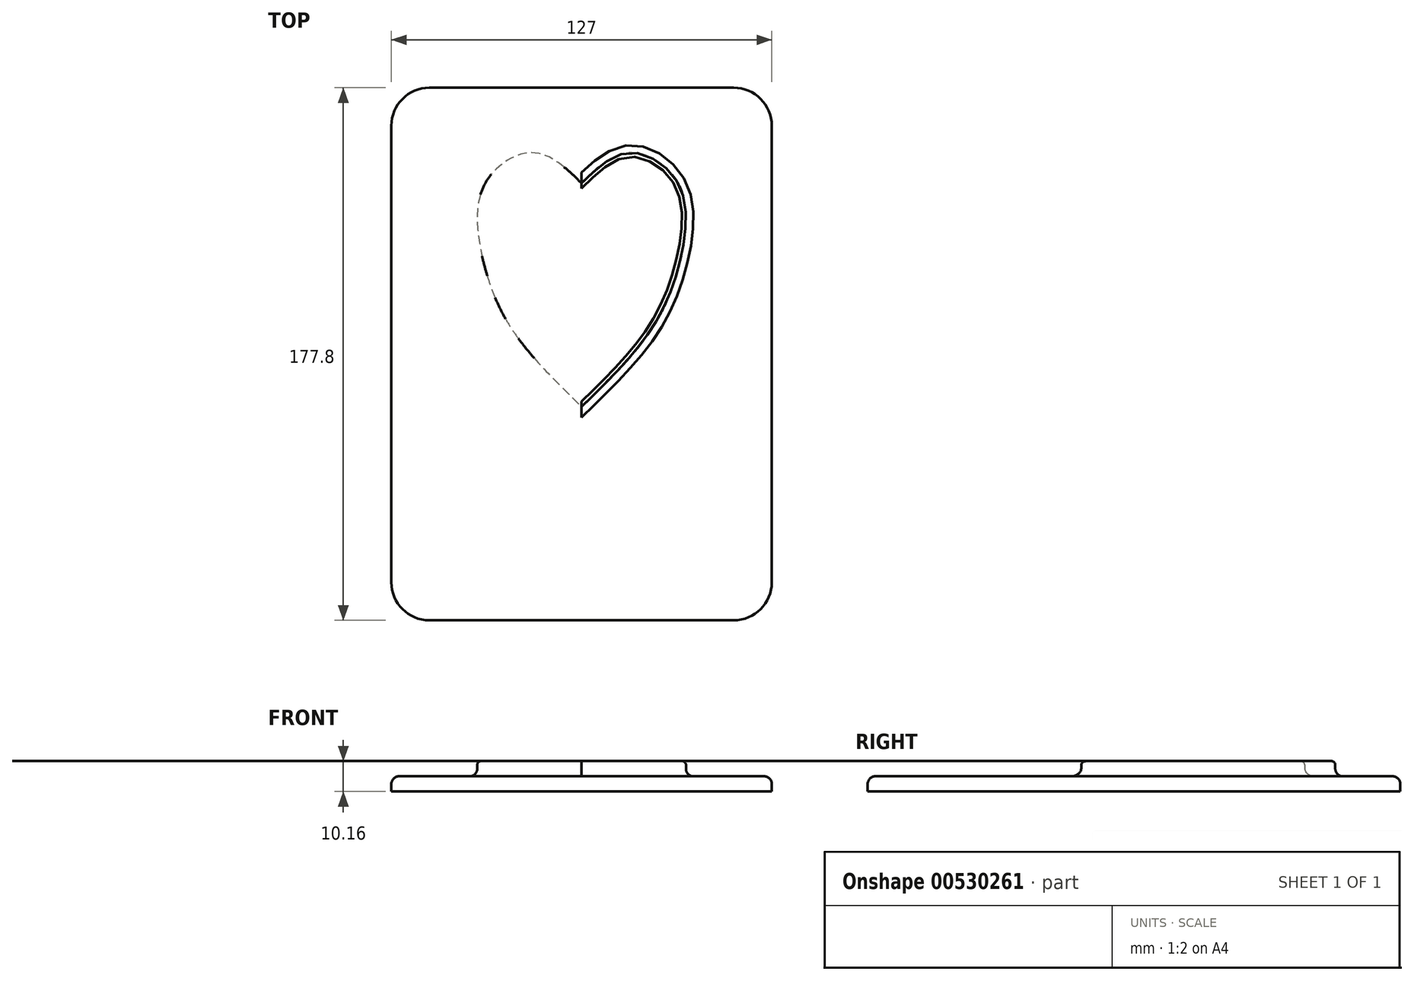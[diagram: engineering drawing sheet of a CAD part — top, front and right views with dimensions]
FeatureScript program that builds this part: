
annotation { "Feature Type Name" : "Feature", "Feature Type Description" : "" }
export const myFeature = defineFeature(function(context is Context, id is Id, definition is map)
    precondition{}
    {
        {
            var Q0;
            Q0=qCreatedBy(makeId("Top.planeOp"),FACE);
            var sketch = newSketch(context, id + "F0", { "sketchPlane" : qUnion([Q0])});
            skLineSegment(sketch, "E0", {"start": v(12.7, 0) * mm, "end": v(114.3, 0) * mm});
            skLineSegment(sketch, "E1", {"start": v(127, 12.7) * mm, "end": v(127, 165.1) * mm});
            skLineSegment(sketch, "E2", {"start": v(114.3, 177.8) * mm, "end": v(12.7, 177.8) * mm});
            skLineSegment(sketch, "E3", {"start": v(0, 165.1) * mm, "end": v(0, 12.7) * mm});
            skPoint(sketch, "E4.visualSharp", {"position": v(0, 177.8) * mm});
            skArc(sketch, "E4.filletArc", {"start": v(12.7, 177.8) * mm, "mid": v(3.72, 174.08) * mm, "end": v(0, 165.1) * mm});
            skPoint(sketch, "E5.visualSharp", {"position": v(127, 177.8) * mm});
            skArc(sketch, "E5.filletArc", {"start": v(127, 165.1) * mm, "mid": v(123.28, 174.08) * mm, "end": v(114.3, 177.8) * mm});
            skPoint(sketch, "E6.visualSharp", {"position": v(0, 0) * mm});
            skArc(sketch, "E6.filletArc", {"start": v(0, 12.7) * mm, "mid": v(3.72, 3.72) * mm, "end": v(12.7, 0) * mm});
            skPoint(sketch, "E7.visualSharp", {"position": v(127, 0) * mm});
            skArc(sketch, "E7.filletArc", {"start": v(114.3, 0) * mm, "mid": v(123.28, 3.72) * mm, "end": v(127, 12.7) * mm});
            skSolve(sketch);
        }
        {
            var Q0;
            Q0 = qSketchRegion(id + "F0", true);
            extrude(context, id + "F1", {"entities" : qUnion([Q0]), "depth" : 5.08 * mm, "offsetDistance" : 25.4 * mm});
        }
        {
            var Q0;
            Q0=makeQuery(id+"F1.opExtrude","CAP_FACE",FACE,{"disambiguationData":[OSD([sQuery(id+"F0.wireOp",EDGE,"E0"),sQuery(id+"F0.wireOp",EDGE,"E1"),sQuery(id+"F0.wireOp",EDGE,"E2"),sQuery(id+"F0.wireOp",EDGE,"E3"),sQuery(id+"F0.wireOp",EDGE,"E4.filletArc"),sQuery(id+"F0.wireOp",EDGE,"E5.filletArc"),sQuery(id+"F0.wireOp",EDGE,"E6.filletArc"),sQuery(id+"F0.wireOp",EDGE,"E7.filletArc")])],"isStart":false});
            var sketch = newSketch(context, id + "F2", { "sketchPlane" : qUnion([Q0])});
            skFitSpline(sketch, "E8", {"points": [v(63.5, 145.94) * mm, v(79.78, 156.1) * mm, v(95.98, 145.3) * mm, v(96.62, 121.16) * mm, v(89, 100.83) * mm, v(77.56, 85.59) * mm, v(63.5, 71.3) * mm], "startDerivative": vector(95.68, 92.94) * mm, "endDerivative": vector(-87.77, -85.87) * mm});
            skFitSpline(sketch, "E9.MirrorCS", {"points": [v(63.5, 145.94) * mm, v(47.22, 156.1) * mm, v(31.02, 145.3) * mm, v(30.38, 121.16) * mm, v(38, 100.83) * mm, v(49.44, 85.59) * mm, v(63.5, 71.3) * mm], "startDerivative": vector(-95.68, 92.94) * mm, "endDerivative": vector(87.77, -85.87) * mm});
            skSolve(sketch);
        }
        {
            var Q0;
            Q0=makeQuery(id+"F2.imprint","IMPRINT",FACE,{"disambiguationData":[TD([[makeQuery(id+"F2.imprint","IMPRINT",EDGE,{"derivedFrom":sQuery(id+"F2.wireOp",EDGE,"E8")}),-1.0]])]});
            extrude(context, id + "F3", {"entities" : qUnion([Q0]), "operationType" : NewBodyOperationType.ADD, "depth" : 5.08 * mm, "offsetDistance" : 25.4 * mm});
        }
        {
            var Q0;
            Q0=makeQuery(id+"F3.opExtrude","CAP_FACE",FACE,{"disambiguationData":[OSD([sQuery(id+"F2.wireOp",EDGE,"E8"),sQuery(id+"F2.wireOp",EDGE,"E9.MirrorCS")])],"isStart":false});
            fillet(context, id + "F4", {"entities" : qUnion([Q0]), "radius" : 1.27 * mm, "tangentPropagation" : true, "allowEdgeOverflow" : false});
        }
        {
            var Q0;
            Q0=makeQuery(id+"F1.opExtrude","CAP_FACE",FACE,{"disambiguationData":[OSD([sQuery(id+"F0.wireOp",EDGE,"E0"),sQuery(id+"F0.wireOp",EDGE,"E1"),sQuery(id+"F0.wireOp",EDGE,"E2"),sQuery(id+"F0.wireOp",EDGE,"E3"),sQuery(id+"F0.wireOp",EDGE,"E4.filletArc"),sQuery(id+"F0.wireOp",EDGE,"E5.filletArc"),sQuery(id+"F0.wireOp",EDGE,"E6.filletArc"),sQuery(id+"F0.wireOp",EDGE,"E7.filletArc")])],"isStart":false});
            fillet(context, id + "F5", {"entities" : qUnion([Q0]), "radius" : 2.54 * mm, "tangentPropagation" : true, "allowEdgeOverflow" : false});
        }
    });
